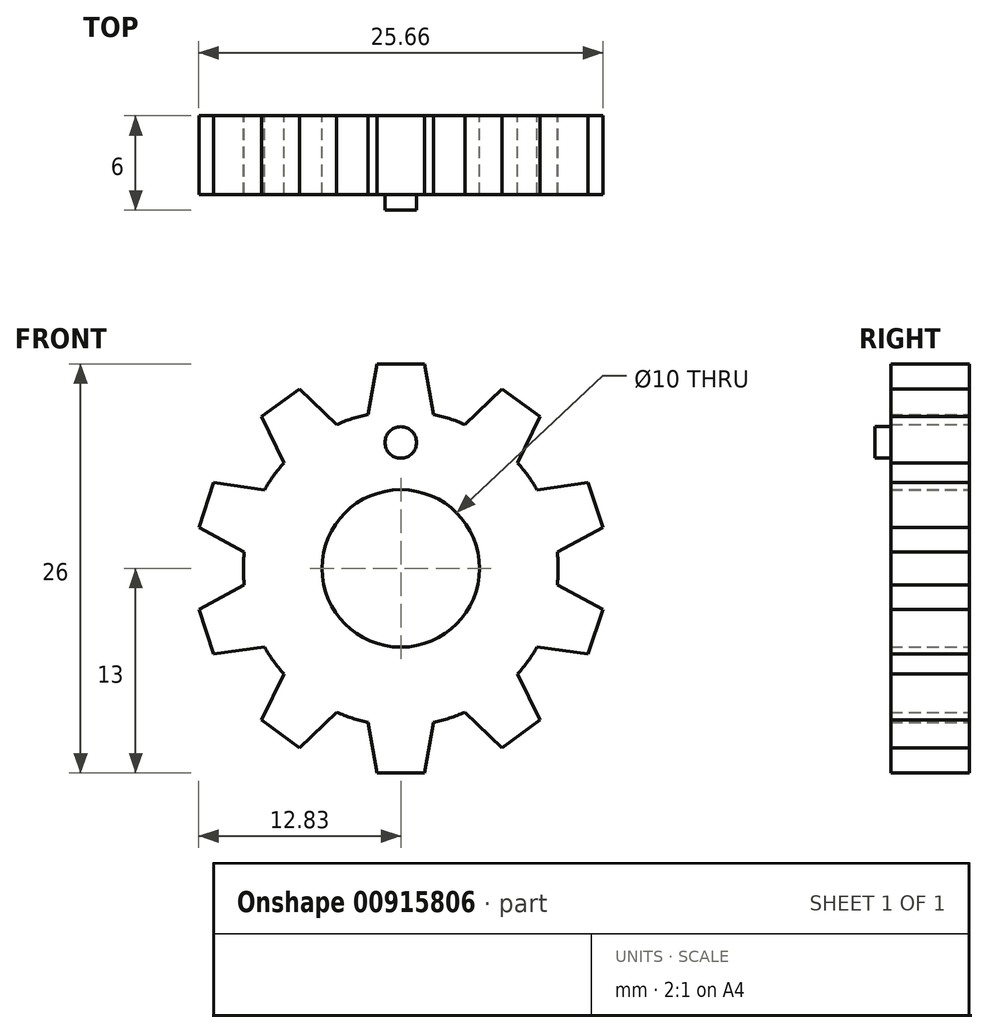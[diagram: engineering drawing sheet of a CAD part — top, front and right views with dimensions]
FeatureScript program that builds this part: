
annotation { "Feature Type Name" : "Feature", "Feature Type Description" : "" }
export const myFeature = defineFeature(function(context is Context, id is Id, definition is map)
    precondition{}
    {
        {
            var Q0;
            Q0=qCreatedBy(makeId("Front.planeOp"),FACE);
            var sketch = newSketch(context, id + "F0", { "sketchPlane" : qUnion([Q0])});
            skCircle(sketch, "E0", {"center": v(0, 0) * mm, "radius": 5 * mm});
            skCircle(sketch, "E1", {"center": v(0, 0) * mm, "radius": 10 * mm});
            skLineSegment(sketch, "E2", {"start": v(-1.5, 13) * mm, "end": v(1.5, 13) * mm});
            skLineSegment(sketch, "E3", {"start": v(1.5, 13) * mm, "end": v(2.07, 9.78) * mm});
            skLineSegment(sketch, "E4.MirrorCS", {"start": v(-1.5, 13) * mm, "end": v(-2.07, 9.78) * mm});
            skLineSegment(sketch, "E5.1.0", {"start": v(-6.43, 11.4) * mm, "end": v(-4.08, 9.13) * mm});
            skLineSegment(sketch, "E5.1.1", {"start": v(-8.85, 9.64) * mm, "end": v(-6.43, 11.4) * mm});
            skLineSegment(sketch, "E5.1.2", {"start": v(-8.85, 9.64) * mm, "end": v(-7.42, 6.7) * mm});
            skLineSegment(sketch, "E5.2.0", {"start": v(-11.9, 5.44) * mm, "end": v(-8.67, 4.99) * mm});
            skLineSegment(sketch, "E5.2.1", {"start": v(-12.83, 2.6) * mm, "end": v(-11.9, 5.44) * mm});
            skLineSegment(sketch, "E5.2.2", {"start": v(-12.83, 2.6) * mm, "end": v(-9.94, 1.06) * mm});
            skLineSegment(sketch, "E6.2.3.0", {"start": v(-12.83, -2.6) * mm, "end": v(-9.94, -1.06) * mm});
            skLineSegment(sketch, "E6.3.3.0", {"start": v(-11.9, -5.44) * mm, "end": v(-12.83, -2.6) * mm});
            skLineSegment(sketch, "E6.6.3.0", {"start": v(-11.9, -5.44) * mm, "end": v(-8.67, -4.99) * mm});
            skLineSegment(sketch, "E6.2.4.0", {"start": v(-8.85, -9.64) * mm, "end": v(-7.42, -6.7) * mm});
            skLineSegment(sketch, "E6.3.4.0", {"start": v(-6.43, -11.4) * mm, "end": v(-8.85, -9.64) * mm});
            skLineSegment(sketch, "E6.6.4.0", {"start": v(-6.43, -11.4) * mm, "end": v(-4.08, -9.13) * mm});
            skLineSegment(sketch, "E6.2.5.0", {"start": v(-1.5, -13) * mm, "end": v(-2.07, -9.78) * mm});
            skLineSegment(sketch, "E6.3.5.0", {"start": v(1.5, -13) * mm, "end": v(-1.5, -13) * mm});
            skLineSegment(sketch, "E6.6.5.0", {"start": v(1.5, -13) * mm, "end": v(2.07, -9.78) * mm});
            skLineSegment(sketch, "E6.2.6.0", {"start": v(6.43, -11.4) * mm, "end": v(4.08, -9.13) * mm});
            skLineSegment(sketch, "E6.3.6.0", {"start": v(8.85, -9.64) * mm, "end": v(6.43, -11.4) * mm});
            skLineSegment(sketch, "E6.6.6.0", {"start": v(8.85, -9.64) * mm, "end": v(7.42, -6.7) * mm});
            skLineSegment(sketch, "E6.2.7.0", {"start": v(11.9, -5.44) * mm, "end": v(8.67, -4.99) * mm});
            skLineSegment(sketch, "E6.3.7.0", {"start": v(12.83, -2.6) * mm, "end": v(11.9, -5.44) * mm});
            skLineSegment(sketch, "E6.6.7.0", {"start": v(12.83, -2.6) * mm, "end": v(9.94, -1.06) * mm});
            skLineSegment(sketch, "E6.2.8.0", {"start": v(12.83, 2.6) * mm, "end": v(9.94, 1.06) * mm});
            skLineSegment(sketch, "E6.3.8.0", {"start": v(11.9, 5.44) * mm, "end": v(12.83, 2.6) * mm});
            skLineSegment(sketch, "E6.6.8.0", {"start": v(11.9, 5.44) * mm, "end": v(8.67, 4.99) * mm});
            skLineSegment(sketch, "E6.2.9.0", {"start": v(8.85, 9.64) * mm, "end": v(7.42, 6.7) * mm});
            skLineSegment(sketch, "E6.3.9.0", {"start": v(6.43, 11.4) * mm, "end": v(8.85, 9.64) * mm});
            skLineSegment(sketch, "E6.6.9.0", {"start": v(6.43, 11.4) * mm, "end": v(4.08, 9.13) * mm});
            skSolve(sketch);
        }
        {
            var Q0;
            Q0 = qSketchRegion(id + "F0", true);
            extrude(context, id + "F1", {"entities" : qUnion([Q0]), "depth" : 5 * mm, "offsetDistance" : 25 * mm});
        }
        {
            var Q0;
            Q0=makeQuery(id+"F1.opExtrude","CAP_FACE",FACE,{"disambiguationData":[OSD([sQuery(id+"F0.wireOp",EDGE,"E0"),sQuery(id+"F0.wireOp",EDGE,"E1"),sQuery(id+"F0.wireOp",EDGE,"E2"),sQuery(id+"F0.wireOp",EDGE,"E3"),sQuery(id+"F0.wireOp",EDGE,"E4.MirrorCS"),sQuery(id+"F0.wireOp",EDGE,"E5.1.0"),sQuery(id+"F0.wireOp",EDGE,"E5.1.1"),sQuery(id+"F0.wireOp",EDGE,"E5.1.2"),sQuery(id+"F0.wireOp",EDGE,"E5.2.0"),sQuery(id+"F0.wireOp",EDGE,"E5.2.1"),sQuery(id+"F0.wireOp",EDGE,"E5.2.2"),sQuery(id+"F0.wireOp",EDGE,"E6.2.3.0"),sQuery(id+"F0.wireOp",EDGE,"E6.3.3.0"),sQuery(id+"F0.wireOp",EDGE,"E6.6.3.0"),sQuery(id+"F0.wireOp",EDGE,"E6.2.4.0"),sQuery(id+"F0.wireOp",EDGE,"E6.3.4.0"),sQuery(id+"F0.wireOp",EDGE,"E6.6.4.0"),sQuery(id+"F0.wireOp",EDGE,"E6.2.5.0"),sQuery(id+"F0.wireOp",EDGE,"E6.3.5.0"),sQuery(id+"F0.wireOp",EDGE,"E6.6.5.0"),sQuery(id+"F0.wireOp",EDGE,"E6.2.6.0"),sQuery(id+"F0.wireOp",EDGE,"E6.3.6.0"),sQuery(id+"F0.wireOp",EDGE,"E6.6.6.0"),sQuery(id+"F0.wireOp",EDGE,"E6.2.7.0"),sQuery(id+"F0.wireOp",EDGE,"E6.3.7.0"),sQuery(id+"F0.wireOp",EDGE,"E6.6.7.0"),sQuery(id+"F0.wireOp",EDGE,"E6.2.8.0"),sQuery(id+"F0.wireOp",EDGE,"E6.3.8.0"),sQuery(id+"F0.wireOp",EDGE,"E6.6.8.0"),sQuery(id+"F0.wireOp",EDGE,"E6.2.9.0"),sQuery(id+"F0.wireOp",EDGE,"E6.3.9.0"),sQuery(id+"F0.wireOp",EDGE,"E6.6.9.0")])],"isStart":false});
            var sketch = newSketch(context, id + "F2", { "sketchPlane" : qUnion([Q0])});
            skCircle(sketch, "E7", {"center": v(0, 8) * mm, "radius": 1 * mm});
            skSolve(sketch);
        }
        {
            var Q0;
            Q0 = qSketchRegion(id + "F2", true);
            extrude(context, id + "F3", {"entities" : qUnion([Q0]), "operationType" : NewBodyOperationType.ADD, "depth" : 1 * mm, "offsetDistance" : 25 * mm});
        }
    });
